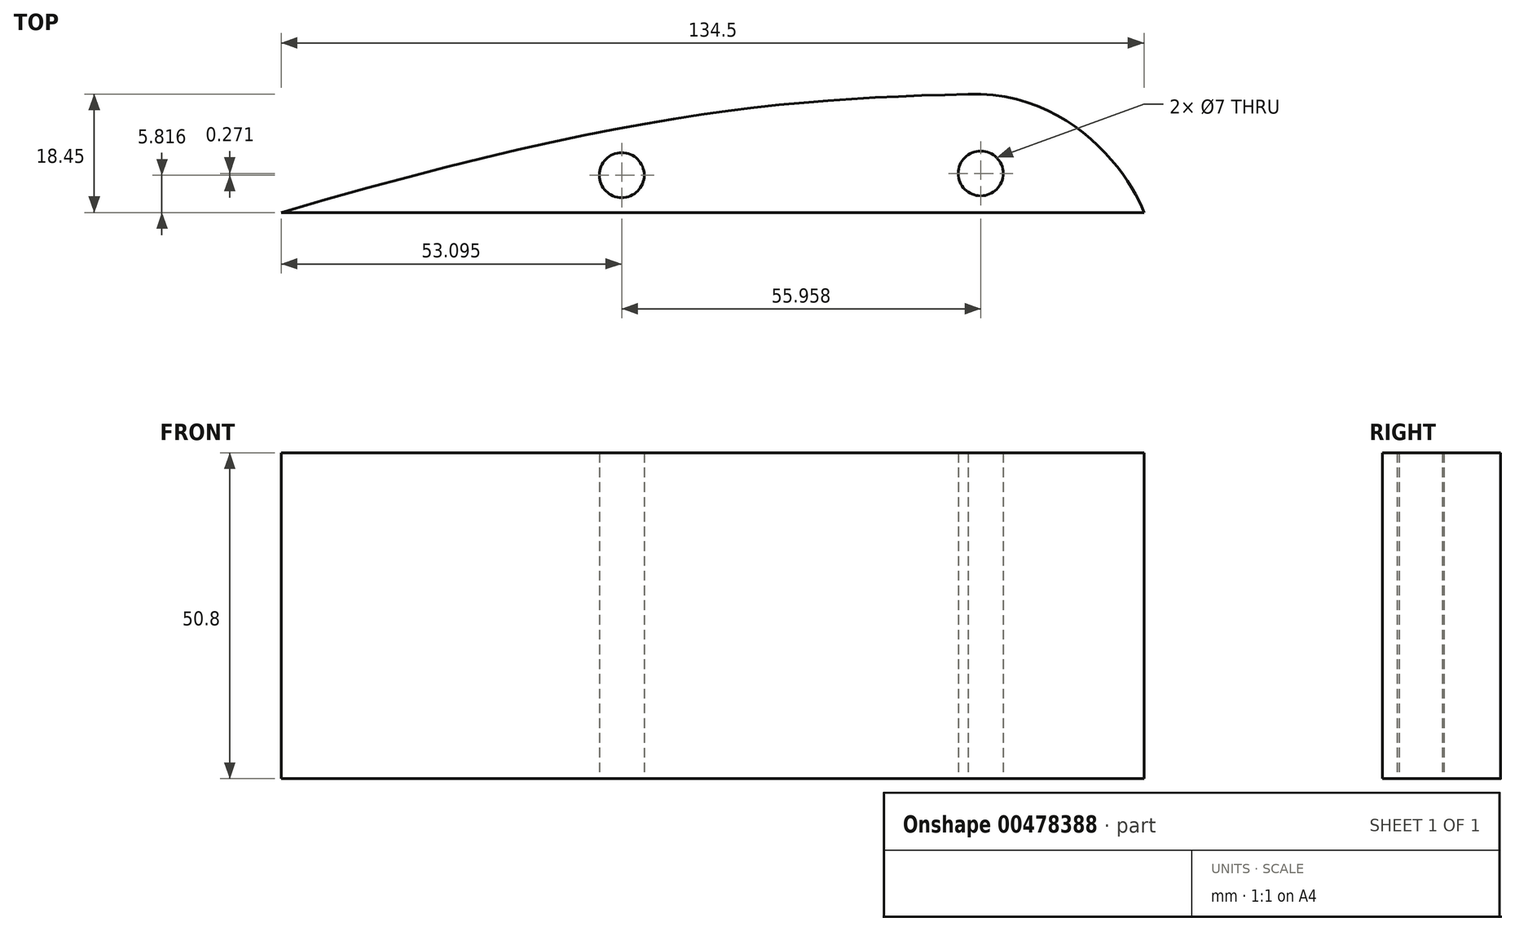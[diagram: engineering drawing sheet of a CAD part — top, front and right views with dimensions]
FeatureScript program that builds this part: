
annotation { "Feature Type Name" : "Feature", "Feature Type Description" : "" }
export const myFeature = defineFeature(function(context is Context, id is Id, definition is map)
    precondition{}
    {
        {
            var Q0;
            Q0=qCreatedBy(makeId("Top.planeOp"),FACE);
            var sketch = newSketch(context, id + "F0", { "sketchPlane" : qUnion([Q0])});
            skLineSegment(sketch, "E0.bottom", {"start": v(-60.73, 0) * mm, "end": v(73.77, 0) * mm});
            skLineSegment(sketch, "E0.right", {"start": v(73.77, 0) * mm, "end": v(73.77, 0) * mm});
            skFitSpline(sketch, "E1", {"points": [v(-60.73, 0) * mm, v(46.36, 18.42) * mm], "startDerivative": vector(162.15, 47.49) * mm, "endDerivative": vector(83.75, 1.73) * mm});
            skPoint(sketch, "E2.orphan", {"position": v(30.07, 18.42) * mm});
            skCircle(sketch, "E3", {"center": v(-7.64, 5.82) * mm, "radius": 3.5 * mm});
            skCircle(sketch, "E4", {"center": v(48.32, 6.09) * mm, "radius": 3.5 * mm});
            skFitSpline(sketch, "E5", {"points": [v(46.36, 18.42) * mm, v(73.77, 0) * mm], "startDerivative": vector(45.9, 2.1) * mm, "endDerivative": vector(7.37, -19.86) * mm});
            skSolve(sketch);
        }
        {
            var Q0;
            Q0=makeQuery(id+"F0.imprint","IMPRINT",FACE,{"disambiguationData":[TD([[makeQuery(id+"F0.imprint","IMPRINT",EDGE,{"derivedFrom":sQuery(id+"F0.wireOp",EDGE,"E0.bottom")}),1.0]])]});
            extrude(context, id + "F1", {"entities" : qUnion([Q0]), "depth" : 50.8 * mm, "offsetDistance" : 25.4 * mm});
        }
    });
